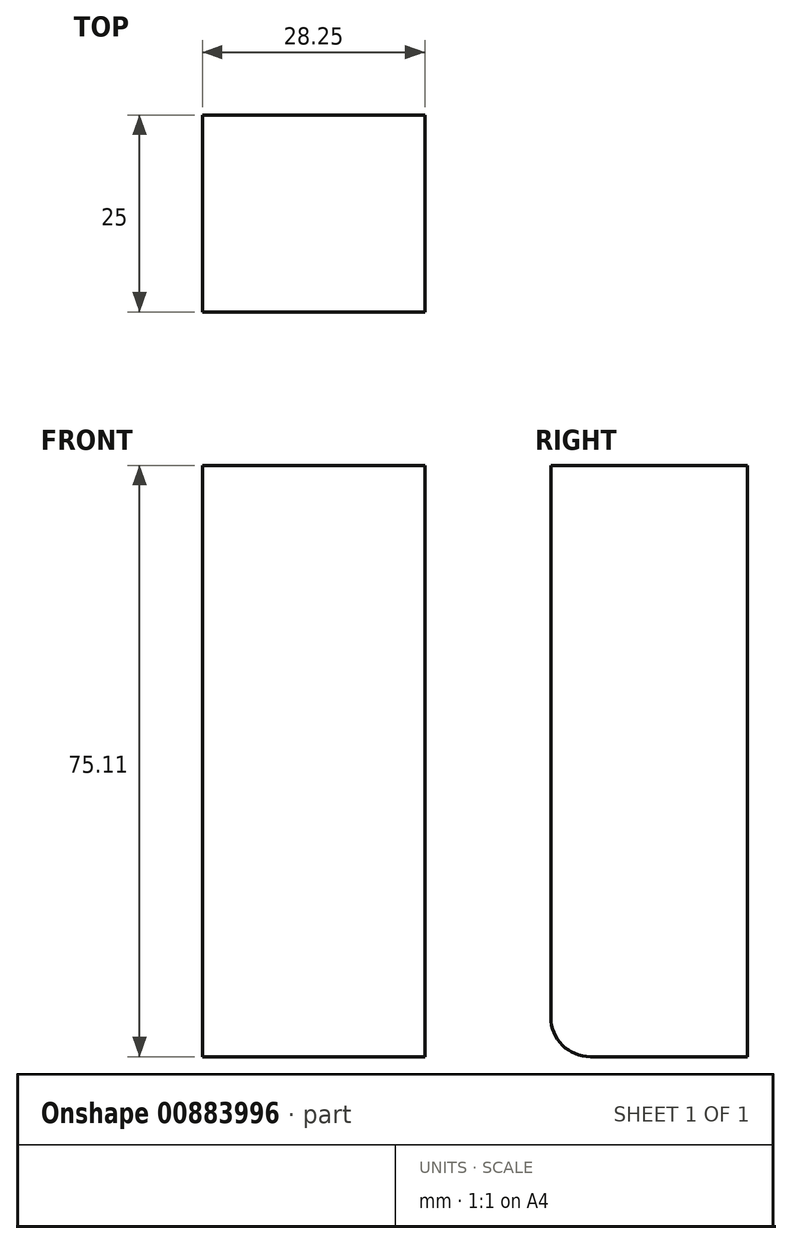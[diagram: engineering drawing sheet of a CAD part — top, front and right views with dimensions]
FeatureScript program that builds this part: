
annotation { "Feature Type Name" : "Feature", "Feature Type Description" : "" }
export const myFeature = defineFeature(function(context is Context, id is Id, definition is map)
    precondition{}
    {
        {
            var Q0;
            Q0=qCreatedBy(makeId("Front.planeOp"),FACE);
            var sketch = newSketch(context, id + "F0", { "sketchPlane" : qUnion([Q0])});
            skLineSegment(sketch, "E0.bottom", {"start": v(-98.16, 34.33) * mm, "end": v(-23.74, 34.33) * mm});
            skLineSegment(sketch, "E0.top", {"start": v(-98.16, -29.53) * mm, "end": v(-23.74, -29.53) * mm});
            skLineSegment(sketch, "E0.left", {"start": v(-98.16, 34.33) * mm, "end": v(-98.16, -29.53) * mm});
            skLineSegment(sketch, "E0.right", {"start": v(-23.74, 34.33) * mm, "end": v(-23.74, -29.53) * mm});
            skSolve(sketch);
        }
        {
            var Q0;
            Q0=qCreatedBy(makeId("Front.planeOp"),FACE);
            var sketch = newSketch(context, id + "F1", { "sketchPlane" : qUnion([Q0])});
            skLineSegment(sketch, "E1.bottom", {"start": v(42.7, 89.84) * mm, "end": v(70.96, 89.84) * mm});
            skLineSegment(sketch, "E1.top", {"start": v(42.7, 164.95) * mm, "end": v(70.96, 164.95) * mm});
            skLineSegment(sketch, "E1.left", {"start": v(42.7, 89.84) * mm, "end": v(42.7, 164.95) * mm});
            skLineSegment(sketch, "E1.right", {"start": v(70.96, 89.84) * mm, "end": v(70.96, 164.95) * mm});
            skSolve(sketch);
        }
        {
            var Q0;
            Q0 = qSketchRegion(id + "F1", true);
            extrude(context, id + "F2", {"entities" : qUnion([Q0]), "depth" : 25 * mm, "offsetDistance" : 25 * mm});
        }
        {
            var Q0;
            Q0=makeQuery(id+"FuqNVuGykSpeb3u_0.opExtrude","SWEPT_EDGE",EDGE,{"disambiguationData":[OSD([sQuery(id+"F0.wireOp",EDGE,"E0.top"),sQuery(id+"F0.wireOp",EDGE,"E0.right")])]});
            var Q1;
            Q1=makeQuery(id+"FuqNVuGykSpeb3u_0.opExtrude","SWEPT_EDGE",EDGE,{"disambiguationData":[OSD([sQuery(id+"F0.wireOp",EDGE,"E0.bottom"),sQuery(id+"F0.wireOp",EDGE,"E0.left")])]});
            var Q2;
            Q2=makeQuery(id+"FuqNVuGykSpeb3u_0.opExtrude","CAP_EDGE",EDGE,{"disambiguationData":[OSD([sQuery(id+"F0.wireOp",EDGE,"E0.left")])],"isStart":false});
            var Q3;
            Q3=makeQuery(id+"FuqNVuGykSpeb3u_0.opExtrude","CAP_EDGE",EDGE,{"disambiguationData":[OSD([sQuery(id+"F0.wireOp",EDGE,"E0.right")])],"isStart":false});
            var Q4;
            Q4=makeQuery(id+"FuqNVuGykSpeb3u_0.opExtrude","SWEPT_EDGE",EDGE,{"disambiguationData":[OSD([sQuery(id+"F0.wireOp",EDGE,"E0.top"),sQuery(id+"F0.wireOp",EDGE,"E0.left")])]});
            var Q5;
            Q5=makeQuery(id+"FuqNVuGykSpeb3u_0.opExtrude","CAP_EDGE",EDGE,{"disambiguationData":[OSD([sQuery(id+"F0.wireOp",EDGE,"E0.bottom")])],"isStart":true});
            var Q6;
            Q6=makeQuery(id+"FuqNVuGykSpeb3u_0.opExtrude","SWEPT_EDGE",EDGE,{"disambiguationData":[OSD([sQuery(id+"F0.wireOp",EDGE,"E0.bottom"),sQuery(id+"F0.wireOp",EDGE,"E0.right")])]});
            var Q7;
            Q7=makeQuery(id+"FuqNVuGykSpeb3u_0.opExtrude","CAP_EDGE",EDGE,{"disambiguationData":[OSD([sQuery(id+"F0.wireOp",EDGE,"E0.right")])],"isStart":true});
            var Q8;
            Q8=makeQuery(id+"FuqNVuGykSpeb3u_0.opExtrude","CAP_EDGE",EDGE,{"disambiguationData":[OSD([sQuery(id+"F0.wireOp",EDGE,"E0.top")])],"isStart":true});
            var Q9;
            Q9=makeQuery(id+"FuqNVuGykSpeb3u_0.opExtrude","CAP_EDGE",EDGE,{"disambiguationData":[OSD([sQuery(id+"F0.wireOp",EDGE,"E0.top")])],"isStart":false});
            var Q10;
            Q10=makeQuery(id+"FuqNVuGykSpeb3u_0.opExtrude","CAP_EDGE",EDGE,{"disambiguationData":[OSD([sQuery(id+"F0.wireOp",EDGE,"E0.bottom")])],"isStart":false});
            var Q11;
            Q11=makeQuery(id+"FuqNVuGykSpeb3u_0.opExtrude","CAP_EDGE",EDGE,{"disambiguationData":[OSD([sQuery(id+"F0.wireOp",EDGE,"E0.left")])],"isStart":true});
            var Q12;
            Q12=makeQuery(id+"F2.opExtrude","CAP_EDGE",EDGE,{"disambiguationData":[OSD([sQuery(id+"F1.wireOp",EDGE,"E1.bottom")])],"isStart":false});
            fillet(context, id + "F3", {"entities" : qUnion([Q0, Q1, Q2, Q3, Q4, Q5, Q6, Q7, Q8, Q9, Q10, Q11, Q12]), "radius" : 5 * mm, "tangentPropagation" : true, "allowEdgeOverflow" : false});
        }
    });
